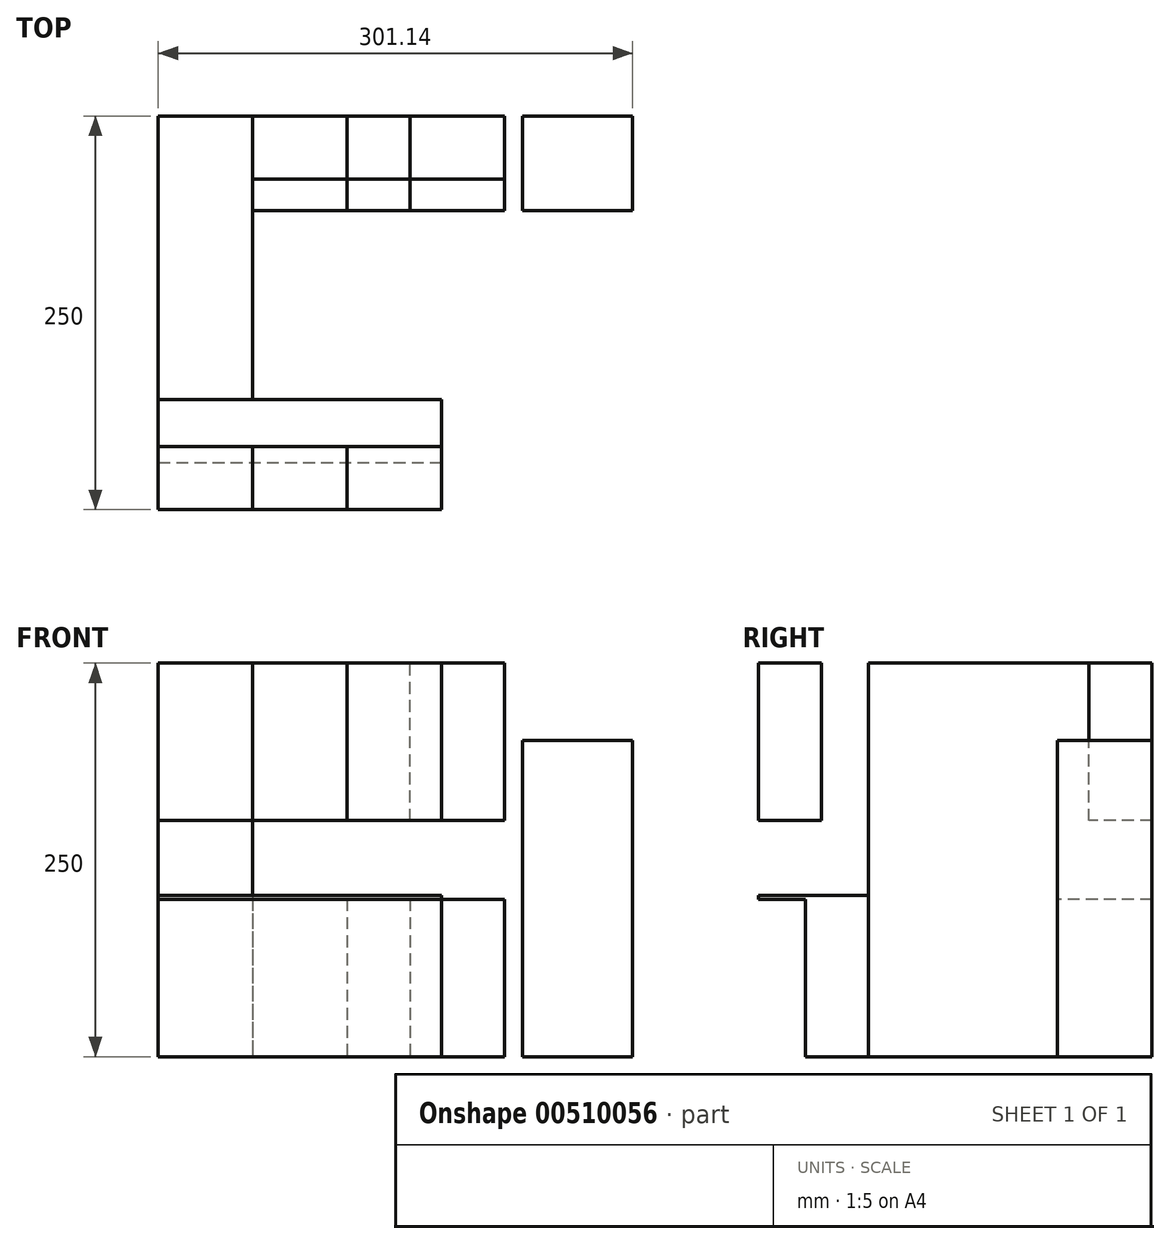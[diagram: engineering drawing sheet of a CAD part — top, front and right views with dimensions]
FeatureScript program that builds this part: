
annotation { "Feature Type Name" : "Feature", "Feature Type Description" : "" }
export const myFeature = defineFeature(function(context is Context, id is Id, definition is map)
    precondition{}
    {
        {
            var Q0;
            Q0=qCreatedBy(makeId("Top.planeOp"),FACE);
            var sketch = newSketch(context, id + "F0", { "sketchPlane" : qUnion([Q0])});
            skLineSegment(sketch, "E0.bottom", {"start": v(0, 0) * mm, "end": v(60, 0) * mm});
            skLineSegment(sketch, "E0.top", {"start": v(0, -120) * mm, "end": v(60, -120) * mm});
            skLineSegment(sketch, "E0.left", {"start": v(0, 0) * mm, "end": v(0, -120) * mm});
            skLineSegment(sketch, "E0.right", {"start": v(60, 0) * mm, "end": v(60, -120) * mm});
            skLineSegment(sketch, "E1.top", {"start": v(0, -180) * mm, "end": v(60, -180) * mm});
            skLineSegment(sketch, "E1.left", {"start": v(0, -120) * mm, "end": v(0, -180) * mm});
            skLineSegment(sketch, "E1.right", {"start": v(60, -120) * mm, "end": v(60, -180) * mm});
            skPoint(sketch, "E2.oppositeSnap0", {"position": v(60, -60) * mm});
            skLineSegment(sketch, "E2.bottom", {"start": v(60, 0) * mm, "end": v(120, 0) * mm});
            skLineSegment(sketch, "E2.top", {"start": v(60, -60) * mm, "end": v(120, -60) * mm});
            skLineSegment(sketch, "E2.left", {"start": v(60, 0) * mm, "end": v(60, -60) * mm});
            skLineSegment(sketch, "E2.right", {"start": v(120, 0) * mm, "end": v(120, -60) * mm});
            skLineSegment(sketch, "E3.bottom", {"start": v(120, 0) * mm, "end": v(160, 0) * mm});
            skLineSegment(sketch, "E3.top", {"start": v(120, -60) * mm, "end": v(160, -60) * mm});
            skLineSegment(sketch, "E3.right", {"start": v(160, 0) * mm, "end": v(160, -60) * mm});
            skLineSegment(sketch, "E4.bottom", {"start": v(160, 0) * mm, "end": v(220, 0) * mm});
            skLineSegment(sketch, "E4.top", {"start": v(160, -60) * mm, "end": v(220, -60) * mm});
            skLineSegment(sketch, "E4.right", {"start": v(220, 0) * mm, "end": v(220, -60) * mm});
            skLineSegment(sketch, "E5.bottom", {"start": v(231.14, 0) * mm, "end": v(301.14, 0) * mm});
            skLineSegment(sketch, "E5.top", {"start": v(231.14, -60) * mm, "end": v(301.14, -60) * mm});
            skLineSegment(sketch, "E5.left", {"start": v(231.14, 0) * mm, "end": v(231.14, -60) * mm});
            skLineSegment(sketch, "E5.right", {"start": v(301.14, 0) * mm, "end": v(301.14, -60) * mm});
            skLineSegment(sketch, "E6.top", {"start": v(0, -220) * mm, "end": v(60, -220) * mm});
            skLineSegment(sketch, "E6.left", {"start": v(0, -180) * mm, "end": v(0, -220) * mm});
            skLineSegment(sketch, "E6.right", {"start": v(60, -180) * mm, "end": v(60, -220) * mm});
            skLineSegment(sketch, "E7.bottom", {"start": v(60, -180) * mm, "end": v(120, -180) * mm});
            skLineSegment(sketch, "E7.top", {"start": v(60, -220) * mm, "end": v(120, -220) * mm});
            skLineSegment(sketch, "E7.right", {"start": v(120, -180) * mm, "end": v(120, -220) * mm});
            skLineSegment(sketch, "E8.bottom", {"start": v(120, -180) * mm, "end": v(180, -180) * mm});
            skLineSegment(sketch, "E8.top", {"start": v(120, -220) * mm, "end": v(180, -220) * mm});
            skLineSegment(sketch, "E8.right", {"start": v(180, -180) * mm, "end": v(180, -220) * mm});
            skSolve(sketch);
        }
        {
            var Q0;
            Q0=makeQuery(id+"F0.imprint","IMPRINT",FACE,{"disambiguationData":[TD([[makeQuery(id+"F0.imprint","IMPRINT",EDGE,{"derivedFrom":sQuery(id+"F0.wireOp",EDGE,"E5.bottom")}),-1.0]])]});
            extrude(context, id + "F1", {"entities" : qUnion([Q0]), "depth" : 201 * mm});
        }
        {
            var Q0;
            Q0=makeQuery(id+"F0.imprint","IMPRINT",FACE,{"disambiguationData":[TD([[makeQuery(id+"F0.imprint","IMPRINT",EDGE,{"derivedFrom":sQuery(id+"F0.wireOp",EDGE,"E4.bottom")}),-1.0]])]});
            extrude(context, id + "F2", {"entities" : qUnion([Q0]), "depth" : 100 * mm});
        }
        {
            var Q0;
            Q0=makeQuery(id+"F0.imprint","IMPRINT",FACE,{"disambiguationData":[TD([[makeQuery(id+"F0.imprint","IMPRINT",EDGE,{"derivedFrom":sQuery(id+"F0.wireOp",EDGE,"E2.bottom")}),-1.0]])]});
            extrude(context, id + "F3", {"entities" : qUnion([Q0]), "depth" : 100 * mm});
        }
        {
            var Q0;
            Q0=makeQuery(id+"F0.imprint","IMPRINT",FACE,{"disambiguationData":[TD([[makeQuery(id+"F0.imprint","IMPRINT",EDGE,{"derivedFrom":sQuery(id+"F0.wireOp",EDGE,"E3.bottom")}),-1.0]])]});
            extrude(context, id + "F4", {"entities" : qUnion([Q0]), "depth" : 100 * mm});
        }
        {
            var Q0;
            Q0=makeQuery(id+"F0.imprint","IMPRINT",FACE,{"disambiguationData":[TD([[makeQuery(id+"F0.imprint","IMPRINT",EDGE,{"derivedFrom":sQuery(id+"F0.wireOp",EDGE,"E0.bottom")}),-1.0]])]});
            extrude(context, id + "F5", {"entities" : qUnion([Q0]), "operationType" : NewBodyOperationType.ADD, "depth" : 250 * mm});
        }
        {
            var Q0;
            Q0=makeQuery(id+"F0.imprint","IMPRINT",FACE,{"disambiguationData":[TD([[makeQuery(id+"F0.imprint","IMPRINT",EDGE,{"derivedFrom":sQuery(id+"F0.wireOp",EDGE,"E0.top")}),-1.0]])]});
            extrude(context, id + "F6", {"entities" : qUnion([Q0]), "operationType" : NewBodyOperationType.ADD, "depth" : 250 * mm});
        }
        {
            var Q0;
            Q0=makeQuery(id+"F0.imprint","IMPRINT",FACE,{"disambiguationData":[TD([[makeQuery(id+"F0.imprint","IMPRINT",EDGE,{"derivedFrom":sQuery(id+"F0.wireOp",EDGE,"E1.top")}),-1.0]])]});
            extrude(context, id + "F7", {"entities" : qUnion([Q0]), "operationType" : NewBodyOperationType.ADD, "depth" : 100 * mm});
        }
        {
            var Q0;
            Q0=makeQuery(id+"F0.imprint","IMPRINT",FACE,{"disambiguationData":[TD([[makeQuery(id+"F0.imprint","IMPRINT",EDGE,{"derivedFrom":sQuery(id+"F0.wireOp",EDGE,"E7.bottom")}),-1.0]])]});
            extrude(context, id + "F8", {"entities" : qUnion([Q0]), "operationType" : NewBodyOperationType.ADD, "depth" : 100 * mm});
        }
        {
            var Q0;
            Q0=makeQuery(id+"F0.imprint","IMPRINT",FACE,{"disambiguationData":[TD([[makeQuery(id+"F0.imprint","IMPRINT",EDGE,{"derivedFrom":sQuery(id+"F0.wireOp",EDGE,"E8.bottom")}),-1.0]])]});
            extrude(context, id + "F9", {"entities" : qUnion([Q0]), "operationType" : NewBodyOperationType.ADD, "depth" : 100 * mm});
        }
        {
            var Q0;
            {var subQ0=sQuery(id+"F0.wireOp",EDGE,"E7.right");var subQ1=sQuery(id+"F0.wireOp",EDGE,"E6.right");Q0=makeQuery(id+"F9.boolean.opBoolean","MERGE",FACE,{"derivedFrom":[makeQuery(id+"F8.boolean.opBoolean","MERGE",FACE,{"derivedFrom":[makeQuery(id+"F7.opExtrude","CAP_FACE",FACE,{"disambiguationData":[OSD([sQuery(id+"F0.wireOp",EDGE,"E1.top"),sQuery(id+"F0.wireOp",EDGE,"E6.top"),sQuery(id+"F0.wireOp",EDGE,"E6.left"),subQ1])],"isStart":false}),makeQuery(id+"F8.opExtrude","CAP_FACE",FACE,{"disambiguationData":[OSD([sQuery(id+"F0.wireOp",EDGE,"E7.bottom"),sQuery(id+"F0.wireOp",EDGE,"E7.top"),subQ1,subQ0])],"isStart":false})]}),makeQuery(id+"F9.opExtrude","CAP_FACE",FACE,{"disambiguationData":[OSD([sQuery(id+"F0.wireOp",EDGE,"E8.bottom"),sQuery(id+"F0.wireOp",EDGE,"E8.top"),subQ0,sQuery(id+"F0.wireOp",EDGE,"E8.right")])],"isStart":false})]});}
            var sketch = newSketch(context, id + "F10", { "sketchPlane" : qUnion([Q0])});
            skLineSegment(sketch, "E9.bottom", {"start": v(180, -180) * mm, "end": v(0, -180) * mm});
            skLineSegment(sketch, "E9.top", {"start": v(180, -250) * mm, "end": v(0, -250) * mm});
            skLineSegment(sketch, "E9.left", {"start": v(180, -180) * mm, "end": v(180, -250) * mm});
            skLineSegment(sketch, "E9.right", {"start": v(0, -180) * mm, "end": v(0, -250) * mm});
            skSolve(sketch);
        }
        {
            var Q0;
            Q0 = qSketchRegion(id + "F10", true);
            extrude(context, id + "F11", {"entities" : qUnion([Q0]), "operationType" : NewBodyOperationType.ADD, "depth" : 2.5 * mm});
        }
        {
            var Q0;
            {var subQ0=sQuery(id+"F0.wireOp",EDGE,"E0.top");Q0=makeQuery(id+"F6.boolean.opBoolean","MERGE",FACE,{"derivedFrom":[makeQuery(id+"F5.opExtrude","CAP_FACE",FACE,{"disambiguationData":[OSD([sQuery(id+"F0.wireOp",EDGE,"E0.bottom"),sQuery(id+"F0.wireOp",EDGE,"E0.left"),sQuery(id+"F0.wireOp",EDGE,"E0.right"),subQ0,sQuery(id+"F0.wireOp",EDGE,"E2.left")])],"isStart":false}),makeQuery(id+"F6.opExtrude","CAP_FACE",FACE,{"disambiguationData":[OSD([subQ0,sQuery(id+"F0.wireOp",EDGE,"E1.left"),sQuery(id+"F0.wireOp",EDGE,"E1.right"),sQuery(id+"F0.wireOp",EDGE,"E1.top")])],"isStart":false})]});}
            var sketch = newSketch(context, id + "F12", { "sketchPlane" : qUnion([Q0])});
            skLineSegment(sketch, "E10.bottom", {"start": v(0, -180) * mm, "end": v(60, -180) * mm});
            skLineSegment(sketch, "E10.top", {"start": v(0, -210) * mm, "end": v(60, -210) * mm});
            skLineSegment(sketch, "E10.left", {"start": v(0, -180) * mm, "end": v(0, -210) * mm});
            skLineSegment(sketch, "E10.right", {"start": v(60, -180) * mm, "end": v(60, -210) * mm});
            skLineSegment(sketch, "E11.top", {"start": v(0, -250) * mm, "end": v(60, -250) * mm});
            skLineSegment(sketch, "E11.left", {"start": v(0, -210) * mm, "end": v(0, -250) * mm});
            skLineSegment(sketch, "E11.right", {"start": v(60, -210) * mm, "end": v(60, -250) * mm});
            skSolve(sketch);
        }
        {
            var Q0;
            Q0=makeQuery(id+"F12.imprint","IMPRINT",FACE,{"disambiguationData":[TD([[makeQuery(id+"F12.imprint","IMPRINT",EDGE,{"derivedFrom":sQuery(id+"F12.wireOp",EDGE,"E10.top")}),-1.0]])]});
            extrude(context, id + "F13", {"entities" : qUnion([Q0]), "oppositeDirection" : true, "depth" : 100 * mm});
        }
        {
            var Q0;
            Q0=makeQuery(id+"F13.opExtrude","CAP_FACE",FACE,{"disambiguationData":[OSD([sQuery(id+"F12.wireOp",EDGE,"E10.top"),sQuery(id+"F12.wireOp",EDGE,"E11.top"),sQuery(id+"F12.wireOp",EDGE,"E11.left"),sQuery(id+"F12.wireOp",EDGE,"E11.right")])],"isStart":true});
            var sketch = newSketch(context, id + "F14", { "sketchPlane" : qUnion([Q0])});
            skLineSegment(sketch, "E12.bottom", {"start": v(60, -210) * mm, "end": v(120, -210) * mm});
            skLineSegment(sketch, "E12.top", {"start": v(60, -250) * mm, "end": v(120, -250) * mm});
            skLineSegment(sketch, "E12.left", {"start": v(60, -210) * mm, "end": v(60, -250) * mm});
            skLineSegment(sketch, "E12.right", {"start": v(120, -210) * mm, "end": v(120, -250) * mm});
            skSolve(sketch);
        }
        {
            var Q0;
            Q0 = qSketchRegion(id + "F14", true);
            extrude(context, id + "F15", {"entities" : qUnion([Q0]), "oppositeDirection" : true, "depth" : 100 * mm});
        }
        {
            var Q0;
            Q0=makeQuery(id+"F15.opExtrude","CAP_FACE",FACE,{"disambiguationData":[OSD([sQuery(id+"F14.wireOp",EDGE,"E12.bottom"),sQuery(id+"F14.wireOp",EDGE,"E12.top"),sQuery(id+"F14.wireOp",EDGE,"E12.left"),sQuery(id+"F14.wireOp",EDGE,"E12.right")])],"isStart":true});
            var sketch = newSketch(context, id + "F16", { "sketchPlane" : qUnion([Q0])});
            skLineSegment(sketch, "E13.bottom", {"start": v(120, -210) * mm, "end": v(180, -210) * mm});
            skLineSegment(sketch, "E13.top", {"start": v(120, -250) * mm, "end": v(180, -250) * mm});
            skLineSegment(sketch, "E13.left", {"start": v(120, -210) * mm, "end": v(120, -250) * mm});
            skLineSegment(sketch, "E13.right", {"start": v(180, -210) * mm, "end": v(180, -250) * mm});
            skSolve(sketch);
        }
        {
            var Q0;
            Q0 = qSketchRegion(id + "F16", true);
            extrude(context, id + "F17", {"entities" : qUnion([Q0]), "oppositeDirection" : true, "depth" : 100 * mm});
        }
        {
            var Q0;
            {var subQ0=sQuery(id+"F0.wireOp",EDGE,"E0.top");Q0=makeQuery(id+"F6.boolean.opBoolean","MERGE",FACE,{"derivedFrom":[makeQuery(id+"F5.opExtrude","CAP_FACE",FACE,{"disambiguationData":[OSD([sQuery(id+"F0.wireOp",EDGE,"E0.bottom"),sQuery(id+"F0.wireOp",EDGE,"E0.left"),sQuery(id+"F0.wireOp",EDGE,"E0.right"),subQ0,sQuery(id+"F0.wireOp",EDGE,"E2.left")])],"isStart":false}),makeQuery(id+"F6.opExtrude","CAP_FACE",FACE,{"disambiguationData":[OSD([subQ0,sQuery(id+"F0.wireOp",EDGE,"E1.left"),sQuery(id+"F0.wireOp",EDGE,"E1.right"),sQuery(id+"F0.wireOp",EDGE,"E1.top")])],"isStart":false})]});}
            var sketch = newSketch(context, id + "F18", { "sketchPlane" : qUnion([Q0])});
            skLineSegment(sketch, "E14.bottom", {"start": v(60, 0) * mm, "end": v(120, 0) * mm});
            skLineSegment(sketch, "E14.top", {"start": v(60, -40) * mm, "end": v(120, -40) * mm});
            skLineSegment(sketch, "E14.left", {"start": v(60, 0) * mm, "end": v(60, -40) * mm});
            skLineSegment(sketch, "E14.right", {"start": v(120, 0) * mm, "end": v(120, -40) * mm});
            skSolve(sketch);
        }
        {
            var Q0;
            Q0 = qSketchRegion(id + "F18", true);
            extrude(context, id + "F19", {"entities" : qUnion([Q0]), "oppositeDirection" : true, "depth" : 100 * mm});
        }
        {
            var Q0;
            Q0=makeQuery(id+"F19.opExtrude","CAP_FACE",FACE,{"disambiguationData":[OSD([sQuery(id+"F18.wireOp",EDGE,"E14.bottom"),sQuery(id+"F18.wireOp",EDGE,"E14.top"),sQuery(id+"F18.wireOp",EDGE,"E14.left"),sQuery(id+"F18.wireOp",EDGE,"E14.right")])],"isStart":true});
            var sketch = newSketch(context, id + "F20", { "sketchPlane" : qUnion([Q0])});
            skLineSegment(sketch, "E15.bottom", {"start": v(120, 0) * mm, "end": v(160, 0) * mm});
            skLineSegment(sketch, "E15.top", {"start": v(120, -40) * mm, "end": v(160, -40) * mm});
            skLineSegment(sketch, "E15.left", {"start": v(120, 0) * mm, "end": v(120, -40) * mm});
            skLineSegment(sketch, "E15.right", {"start": v(160, 0) * mm, "end": v(160, -40) * mm});
            skSolve(sketch);
        }
        {
            var Q0;
            Q0 = qSketchRegion(id + "F20", true);
            extrude(context, id + "F21", {"entities" : qUnion([Q0]), "oppositeDirection" : true, "depth" : 100 * mm});
        }
        {
            var Q0;
            Q0=makeQuery(id+"F21.opExtrude","CAP_FACE",FACE,{"disambiguationData":[OSD([sQuery(id+"F20.wireOp",EDGE,"E15.bottom"),sQuery(id+"F20.wireOp",EDGE,"E15.top"),sQuery(id+"F20.wireOp",EDGE,"E15.left"),sQuery(id+"F20.wireOp",EDGE,"E15.right")])],"isStart":true});
            var sketch = newSketch(context, id + "F22", { "sketchPlane" : qUnion([Q0])});
            skLineSegment(sketch, "E16.bottom", {"start": v(160, 0) * mm, "end": v(220, 0) * mm});
            skLineSegment(sketch, "E16.top", {"start": v(160, -40) * mm, "end": v(220, -40) * mm});
            skLineSegment(sketch, "E16.left", {"start": v(160, 0) * mm, "end": v(160, -40) * mm});
            skLineSegment(sketch, "E16.right", {"start": v(220, 0) * mm, "end": v(220, -40) * mm});
            skSolve(sketch);
        }
        {
            var Q0;
            Q0 = qSketchRegion(id + "F22", true);
            extrude(context, id + "F23", {"entities" : qUnion([Q0]), "oppositeDirection" : true, "depth" : 100 * mm});
        }
    });
